# Revit family: Seat-Shower-STERLING-Accord-72186104
name_source: partatom
category: Specialty Equipment
revit_build: Autodesk Revit 2015 (Build: 20140606_1530(x64)
units: mm (PartAtom-declared; Revit-internal decimal feet)

## types (2) — shared parameters
ADA Compliant = No
Assembly Code = C1030200
Date Modified = 06/04/2019
Default Elevation = 0"
Description = Freestanding Seat
Height = 17 3/8"
Length = 21 3/8"
Manufacturer = KOHLER Co.
MasterFormat 1995 = 10820
MasterFormat 2004 = 10.28.13
Material = Plastic
Product Documentation Link = https://www.sterlingplumbing.com
Product Name = Accord
Product Page URL = http://www.sterlingplumbing.com
URL = https://www.sterlingplumbing.com
WaterSense Certified = No
Width = 13 1/8"

## per-type parameters (varying)
| type | Finish | Model | Type |
| 96-Biscuit | Kohler-Plastic-96-Biscuit | 72186104-96 | 2 |
| 0-White | Kohler-Plastic-0-White | 72186104-0 | 1 |

## geometry (parser evidence)
native form markers: Sweep x5
no freeform markers — native parametric forms only
